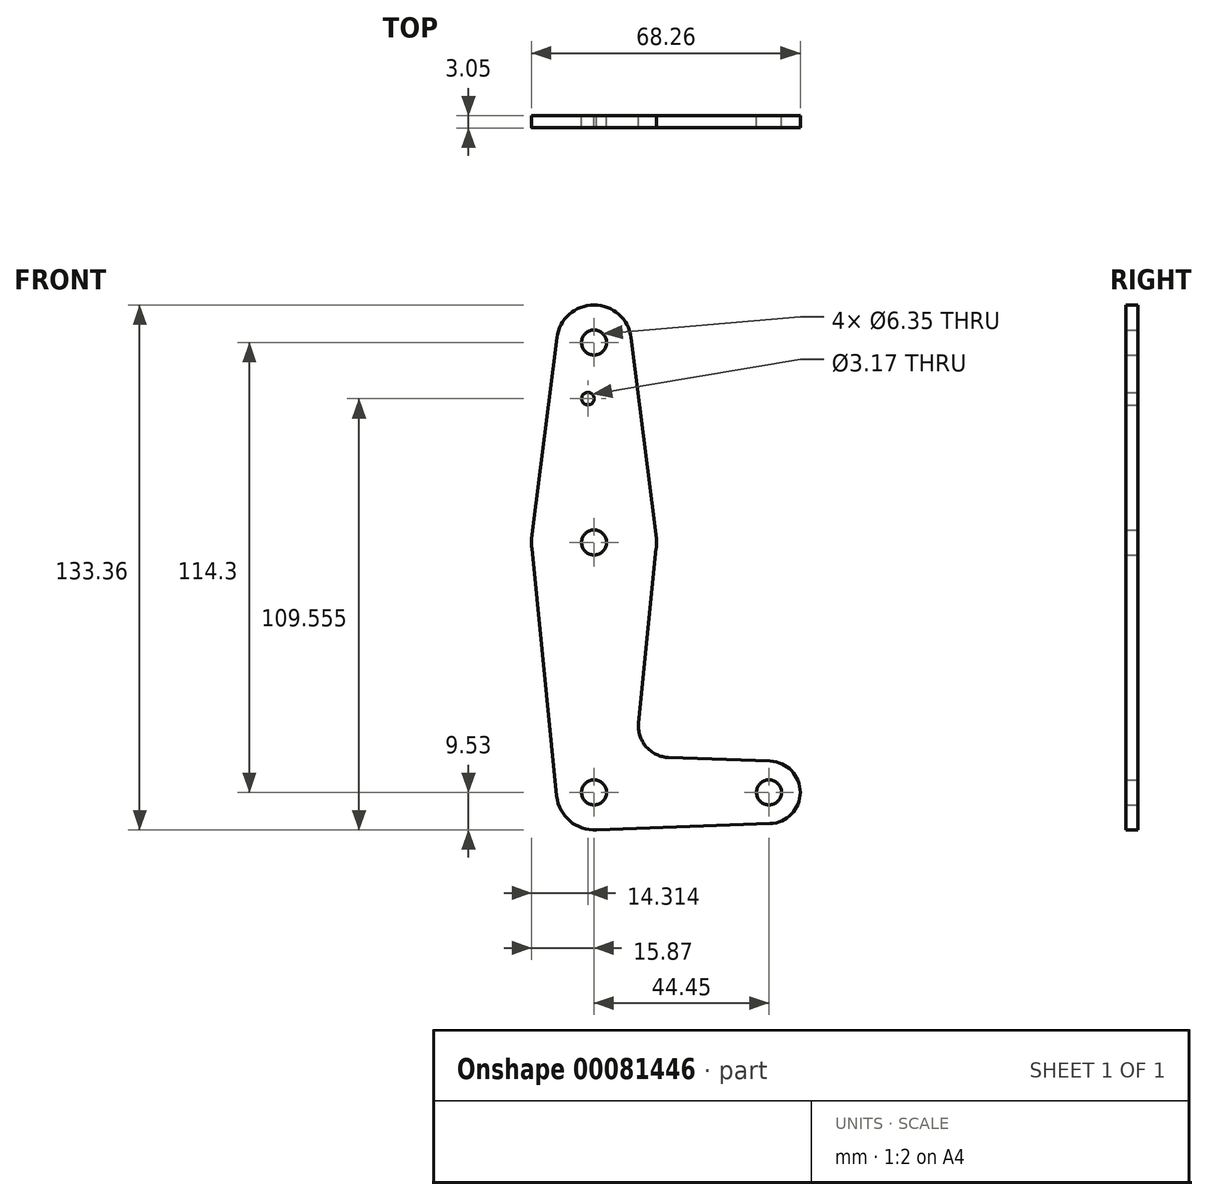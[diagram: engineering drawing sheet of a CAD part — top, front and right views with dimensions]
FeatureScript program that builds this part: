
annotation { "Feature Type Name" : "Feature", "Feature Type Description" : "" }
export const myFeature = defineFeature(function(context is Context, id is Id, definition is map)
    precondition{}
    {
        {
            var Q0;
            Q0=qCreatedBy(makeId("Front.planeOp"),FACE);
            var sketch = newSketch(context, id + "F0", { "sketchPlane" : qUnion([Q0])});
            skCircle(sketch, "E0", {"center": v(0, 0) * mm, "radius": 9.53 * mm});
            skCircle(sketch, "E1", {"center": v(0, 114.3) * mm, "radius": 9.53 * mm});
            skCircle(sketch, "E2", {"center": v(44.45, 0) * mm, "radius": 7.94 * mm});
            skLineSegment(sketch, "E3", {"start": v(0, 0) * mm, "end": v(44.45, 0) * mm, "construction": true});
            skCircle(sketch, "E4", {"center": v(0, 63.5) * mm, "radius": 15.88 * mm});
            skLineSegment(sketch, "E5", {"start": v(0, 114.3) * mm, "end": v(0, 0) * mm, "construction": true});
            skLineSegment(sketch, "E6", {"start": v(-9.45, 115.5) * mm, "end": v(-15.75, 65.48) * mm});
            skLineSegment(sketch, "E7", {"start": v(0, -9.53) * mm, "end": v(44.73, -7.93) * mm});
            skLineSegment(sketch, "E8", {"start": v(18.97, 8.85) * mm, "end": v(44.73, 7.93) * mm});
            skLineSegment(sketch, "E9", {"start": v(15.8, 61.91) * mm, "end": v(11.34, 17.6) * mm});
            skLineSegment(sketch, "E10", {"start": v(9.45, 115.5) * mm, "end": v(15.75, 65.48) * mm});
            skCircle(sketch, "E11", {"center": v(0, 114.3) * mm, "radius": 3.18 * mm});
            skLineSegment(sketch, "E12", {"start": v(0, 63.5) * mm, "end": v(0, 100.03) * mm});
            skLineSegment(sketch, "E13", {"start": v(0, 100.03) * mm, "end": v(-1.56, 100.03) * mm});
            skCircle(sketch, "E14", {"center": v(-1.56, 100.03) * mm, "radius": 1.59 * mm});
            skCircle(sketch, "E15", {"center": v(0, 63.5) * mm, "radius": 3.18 * mm});
            skCircle(sketch, "E16", {"center": v(0, 0) * mm, "radius": 3.18 * mm});
            skCircle(sketch, "E17", {"center": v(44.45, 0) * mm, "radius": 3.18 * mm});
            skArc(sketch, "E18.filletArc", {"start": v(11.34, 17.6) * mm, "mid": v(13.26, 11.57) * mm, "end": v(18.97, 8.85) * mm});
            skLineSegment(sketch, "E19", {"start": v(-15.8, 61.91) * mm, "end": v(-9.48, -0.95) * mm});
            skSolve(sketch);
        }
        {
            var Q0;
            Q0 = qSketchRegion(id + "F0", true);
            extrude(context, id + "F1", {"entities" : qUnion([Q0]), "depth" : 3.05 * mm});
        }
    });
